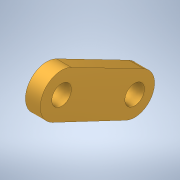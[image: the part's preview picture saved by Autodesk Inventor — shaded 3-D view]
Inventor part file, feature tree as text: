
AUTODESK INVENTOR PART (.ipt)
format: ipt  version: 2020 (Build 240168000, 168)  size: 143,360 bytes
history: native  units: in
note: dims shown in document units (in); Inventor stores cm internally (conversion verified against a paired STEP export)
features: extrude x3, sketch x3, projected_geometry x1
ambient origin geometry x8: Origin, YZ Plane, XZ Plane, XY Plane, X Axis, Y Axis, Z Axis, Center Point
bodies: Solid1 (feature_tree)
feature tree (7):
  extrude  "Extrusion1"  Depth=0.4523in
  extrude  "Extrusion2"  Depth=0.2118in
  extrude  "Extrusion3"  Depth=0.1575in TaperAngle=0.0deg
  sketch  "Sketch1"  dims[d0=0.2087in d1=0.2087in d3=0.4523in]
  sketch  "Sketch2"  dims[d4=0.2118in d5=0.8586in]
  projected_geometry  "Projected Loop1"
  sketch  "Sketch3"  dims[d6=0.8656in d7=0.1575in d8=0.0in d11=0.0787in d12=0.315in d13=0.1575in d14=0.0in d15=0.1969in d16=0.0787in d17=0.0in d20=0.7087in d21=0.4228in]
